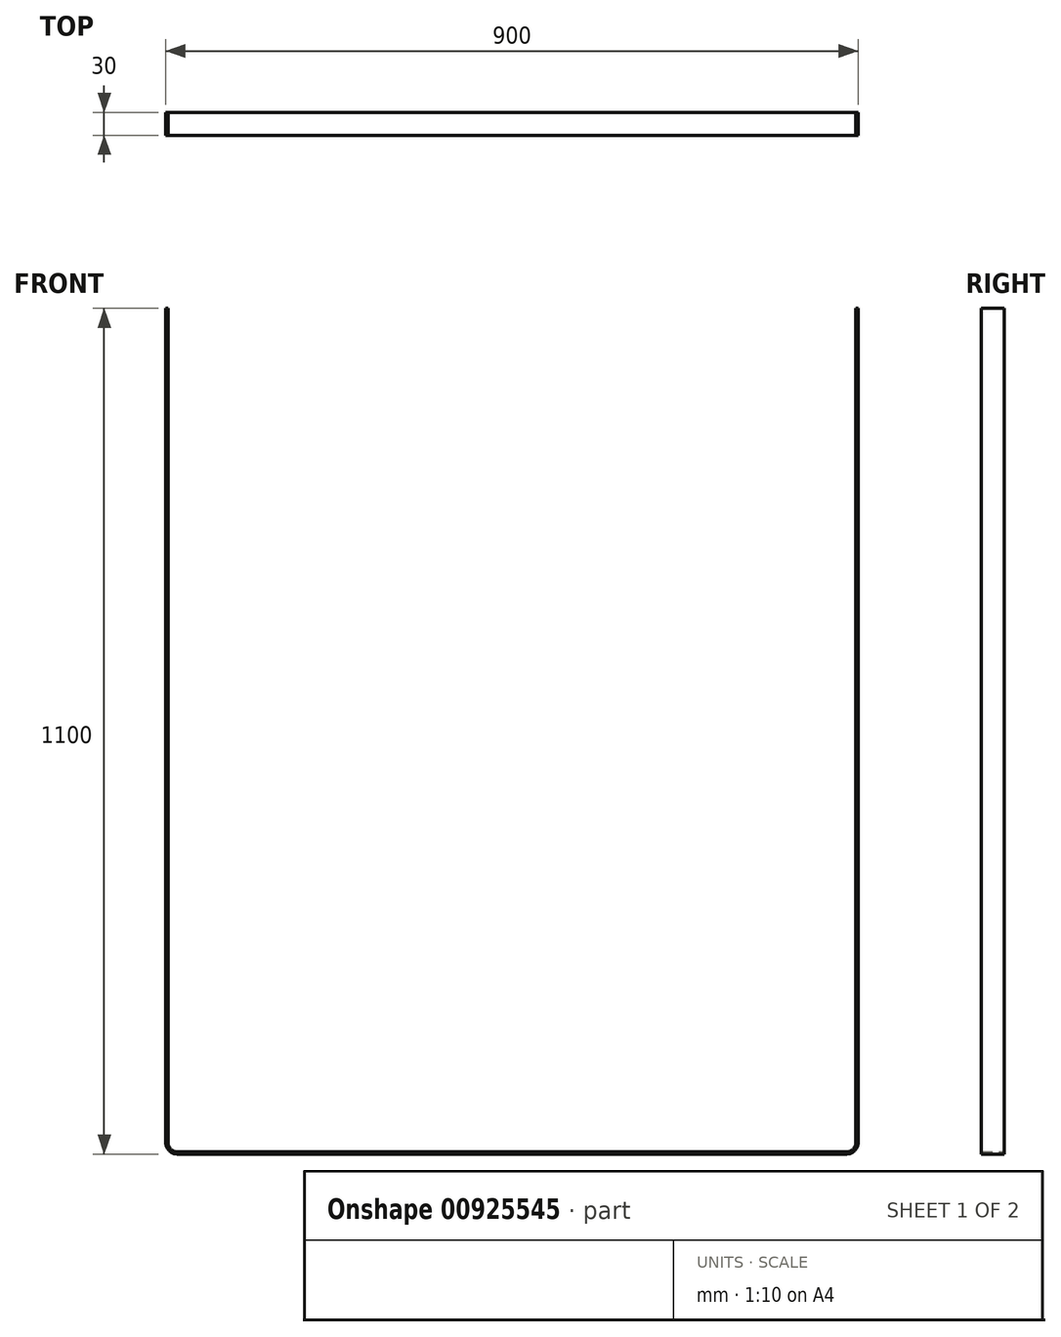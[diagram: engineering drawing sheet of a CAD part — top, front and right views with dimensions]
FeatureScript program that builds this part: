
annotation { "Feature Type Name" : "Feature", "Feature Type Description" : "" }
export const myFeature = defineFeature(function(context is Context, id is Id, definition is map)
    precondition{}
    {
        {
            var Q0;
            Q0=qCreatedBy(makeId("Front.planeOp"),FACE);
            var sketch = newSketch(context, id + "F0", { "sketchPlane" : qUnion([Q0])});
            skLineSegment(sketch, "E0.bottom", {"start": v(435, -550) * mm, "end": v(-435, -550) * mm});
            skLineSegment(sketch, "E0.top", {"start": v(450, 550) * mm, "end": v(447, 550) * mm});
            skLineSegment(sketch, "E0.left", {"start": v(450, -535) * mm, "end": v(450, 550) * mm});
            skLineSegment(sketch, "E0.right", {"start": v(-450, -535) * mm, "end": v(-450, 550) * mm});
            skPoint(sketch, "E0.middle", {"position": v(0, 0) * mm});
            skPoint(sketch, "E1.visualSharp", {"position": v(-450, -550) * mm});
            skArc(sketch, "E1.filletArc", {"start": v(-450, -535) * mm, "mid": v(-445.6, -545.6) * mm, "end": v(-435, -550) * mm});
            skPoint(sketch, "E2.visualSharp", {"position": v(450, -550) * mm});
            skArc(sketch, "E2.filletArc", {"start": v(435, -550) * mm, "mid": v(445.6, -545.6) * mm, "end": v(450, -535) * mm});
            skLineSegment(sketch, "E3.0", {"start": v(-447, -535) * mm, "end": v(-447, 550) * mm});
            skLineSegment(sketch, "E3.1", {"start": v(447, -535) * mm, "end": v(447, 550) * mm});
            skArc(sketch, "E3.2", {"start": v(435, -547) * mm, "mid": v(443.49, -543.49) * mm, "end": v(447, -535) * mm});
            skLineSegment(sketch, "E3.3", {"start": v(435, -547) * mm, "end": v(-435, -547) * mm});
            skArc(sketch, "E3.4", {"start": v(-447, -535) * mm, "mid": v(-443.49, -543.49) * mm, "end": v(-435, -547) * mm});
            skLineSegment(sketch, "E4.trimOffspring", {"start": v(-447, 550) * mm, "end": v(-450, 550) * mm});
            skSolve(sketch);
        }
        {
            var Q0;
            Q0 = qSketchRegion(id + "F0", true);
            extrude(context, id + "F1", {"entities" : qUnion([Q0]), "endBound" : BoundingType.SYMMETRIC, "depth" : 30 * mm, "offsetDistance" : 25 * mm});
        }
    });
